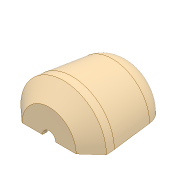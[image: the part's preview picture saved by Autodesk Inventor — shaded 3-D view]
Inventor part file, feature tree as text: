
AUTODESK INVENTOR PART (.ipt)
format: ipt  version: 2017 (Build 210142000, 142)  size: 458,240 bytes
history: native  units: mm
features: sketch x17, extrude x12, projected_geometry x5, fillet x4, chamfer x3, plane x2, revolve x1, thicken_offset x1, shell x1
ambient origin geometry x8: Origin, YZ Plane, XZ Plane, XY Plane, X Axis, Y Axis, Z Axis, Center Point
bodies: Solid1 (feature_tree)
feature tree (46):
  revolve  "Revolution1"  [1 undecoded]
  fillet  "Fillet1"  Radius=30.0mm
  chamfer  "Chamfer1"  Distance=10.0mm Angle=45.0deg
  fillet  "Fillet2"  Radius=20.0mm
  fillet  "Fillet3"  Radius=60.0mm
  thicken_offset  "Thicken1"
  extrude  "Extrusion1"  Depth=4.0mm
  sketch  "Sketch3"  dims[d4=20.0mm d5=10.0mm d6=20.0mm d7=45.0deg d8=20.0mm d9=60.0mm]
  extrude  "Extrusion5"  Depth=50.0mm
  sketch  "Sketch7"  dims[d12=0.0mm d13=0.0mm d14=50.0mm]
  plane  "Work Plane1"
  extrude  "Extrusion6"  Depth=12.0mm
  extrude  "Extrusion7"  Depth=12.0mm
  extrude  "Extrusion8"  Depth=40.0mm
  plane  "Work Plane2"
  extrude  "Extrusion9"  Depth=22.0mm
  sketch  "Sketch12"  dims[d39=4.0mm d40=6.0mm]
  extrude  "Extrusion10"  Depth=6.0mm
  extrude  "Extrusion11"  Depth=20.5mm TaperAngle=0.0deg
  chamfer  "Chamfer2"  Distance=6.0mm
  shell  "Shell2"  Thickness=12.0mm
  extrude  "Extrusion12"  Depth=2.0mm TaperAngle=0.0deg
  extrude  "Extrusion13"  Depth=2.0mm TaperAngle=0.0deg
  sketch  "Sketch17"  dims[d55=10.0mm d56=0.0mm d57=0.0mm]
  extrude  "Extrusion14"  TaperAngle=0.0deg  [1 undecoded]
  fillet  "Fillet8"  Radius=2.0mm
  extrude  "Extrusion15"  Depth=10.0mm TaperAngle=0.0deg
  chamfer  "Chamfer3"  Distance=10.0mm
  sketch  "Sketch1"  dims[d0=40.0mm d1=80.0mm d2=30.0mm]
  sketch  "Sketch2"  dims[d3=90.0deg]
  sketch  "Sketch6"  dims[d10=4.0mm d11=4.0mm]
  sketch  "Sketch8"  dims[d15=12.0mm d16=12.0mm]
  sketch  "Sketch9"  dims[d17=12.0mm d18=12.0mm]
  projected_geometry  "Projected Loop1"
  sketch  "Sketch10"  dims[d34=45.0mm d35=40.0mm]
  projected_geometry  "Projected Loop2"
  sketch  "Sketch11"  dims[d36=40.0mm d37=0.0mm d38=22.0mm]
  sketch  "Sketch13"  dims[d41=-8.0mm d42=20.5mm d43=0.0mm]
  sketch  "Sketch14"  dims[d44=25.0mm d45=6.0mm d46=0.0mm d47=12.0mm d48=0.0mm]
  sketch  "Sketch15"  dims[d49=-3.75mm d50=2.0mm d51=0.0mm]
  projected_geometry  "Projected Loop3"
  sketch  "Sketch16"  dims[d52=28.0mm d53=2.0mm d54=0.0mm]
  projected_geometry  "Projected Loop4"
  sketch  "Sketch18"  dims[d58=11.0mm d59=2.0mm d60=45.0deg d61=2.0mm]
  projected_geometry  "Projected Loop5"
  sketch  "Sketch19"  dims[d62=10.0mm d63=0.0mm d64=10.0mm d65=0.0mm d66=10.0mm d67=0.0mm d68=3.0mm d69=3.0mm d70=10.0mm d71=0.0mm d72=6.0mm d73=2.0mm d74=45.0deg]
note: 2 required parameter values undecoded (feature->parameter linkage not recoverable at this tier; creation-order binding heuristic only, values carry confidence <= 0.55)